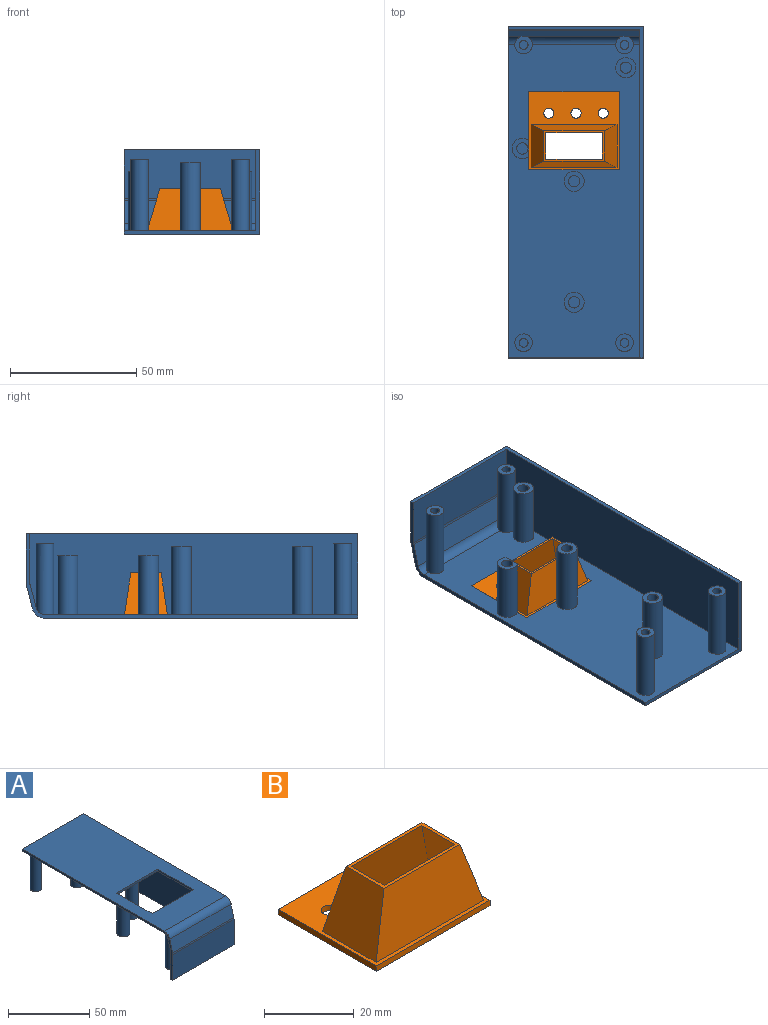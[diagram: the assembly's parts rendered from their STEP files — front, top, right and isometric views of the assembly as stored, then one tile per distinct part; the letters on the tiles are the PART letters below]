
ASSEMBLY  parts=2 mates=1
PART A: 51 faces, bbox 53.5x131.5x33.5 mm
  f0: plane 124.13x52mm, normal (0,0,-1), area 5027mm2, adj f3,f9,f13,f14,f16,f18,f20,f30
  f1: plane 124.13x53.5mm, normal (0,0,1), area 5525mm2, adj f3,f4,f8,f38,f39,f40,f41,f50
  f2: plane 131.5x53.5mm, normal (0,0,-1), area 275.2mm2, adj f3,f7,f8,f12,f13,f50
  f3: plane 53.5x33.5mm, normal (0,1,0), area 128.3mm2, adj f0,f1,f2,f8,f13,f50
  f4: cylinder r=5mm len=53.5mm, axis (-1,0,0), area 352.3mm2, adj f1,f5,f8,f50
  f5: plane 53.5x9.14mm, normal (0,-0.97,0.25), area 505mm2, adj f4,f6,f8,f50
  f6: cylinder r=5mm len=53.5mm, axis (-1,0,0), area 67.9mm2, adj f5,f7,f8,f50
  f7: plane 53.5x19.36mm, normal (0,-1,0), area 1035.9mm2, adj f2,f6,f8,f50
  f8: plane 131.5x33.5mm, normal (1,0,0), area 4378.7mm2, adj f1,f2,f3,f4,f5,f6,f7
  f9: cylinder r=3.5mm len=52mm, axis (-1,0,0), area 195.3mm2, adj f0,f10,f13,f18,f20,f50
  f10: plane 52x9.14mm, normal (0,0.97,-0.25), area 490.9mm2, adj f9,f11,f13,f50
  f11: cylinder r=3.5mm len=52mm, axis (-1,0,0), area 46.2mm2, adj f10,f12,f13,f50
  f12: plane 52x19.36mm, normal (0,1,0), area 1006.8mm2, adj f2,f11,f13,f50
  f13: plane 130x32mm, normal (-1,0,0), area 4139.3mm2, adj f0,f2,f3,f9,f10,f11,f12
  f14: cylinder r=3.5mm len=28.2mm, axis (0,0,1), area 620.2mm2, adj f0,f15
  f15: plane 7x7mm, normal (0,0,-1), area 28.9mm2, adj f14,f28
  f16: cylinder r=3.5mm len=28.2mm, axis (0,0,1), area 620.2mm2, adj f0,f17
  f17: plane 7x7mm, normal (0,0,-1), area 28.9mm2, adj f16,f26
  f18: cylinder r=3.5mm len=28.2mm, axis (0,0,1), area 608.4mm2, adj f0,f9,f19
  f19: plane 7x7mm, normal (0,0,-1), area 28.9mm2, adj f18,f24
  f20: cylinder r=3.5mm len=28.2mm, axis (0,0,1), area 608.4mm2, adj f0,f9,f21
  f21: plane 7x7mm, normal (0,0,-1), area 28.9mm2, adj f20,f22
  f22: cylinder r=1.75mm len=10mm, axis (0,0,-1), area 110mm2, adj f21,f23
  f23: plane 3.5x3.5mm, normal (0,0,-1), area 9.6mm2, adj f22
  f24: cylinder r=1.75mm len=10mm, axis (0,0,-1), area 110mm2, adj f19,f25
  f25: plane 3.5x3.5mm, normal (0,0,-1), area 9.6mm2, adj f24
  f26: cylinder r=1.75mm len=10mm, axis (0,0,-1), area 110mm2, adj f17,f27
  f27: plane 3.5x3.5mm, normal (0,0,-1), area 9.6mm2, adj f26
  f28: cylinder r=1.75mm len=10mm, axis (0,0,-1), area 110mm2, adj f15,f29
  f29: plane 3.5x3.5mm, normal (0,0,-1), area 9.6mm2, adj f28
  f30: cylinder r=4mm len=27mm, axis (0,0,1), area 678.6mm2, adj f0,f31
  f31: plane 8x8mm, normal (0,0,-1), area 34.4mm2, adj f30,f36
  f32: cylinder r=4mm len=27mm, axis (0,0,1), area 678.6mm2, adj f0,f33
  f33: plane 8x8mm, normal (0,0,-1), area 34.4mm2, adj f32,f34
  f34: cylinder r=2.25mm len=10mm, axis (0,0,-1), area 141.4mm2, adj f33,f35
  f35: plane 4.5x4.5mm, normal (0,0,-1), area 15.9mm2, adj f34
  f36: cylinder r=2.25mm len=10mm, axis (0,0,-1), area 141.4mm2, adj f31,f37
  f37: plane 4.5x4.5mm, normal (0,0,-1), area 15.9mm2, adj f36
  f38: plane 36x1.5mm, normal (0,1,0), area 54mm2, adj f0,f1,f39,f41
  f39: plane 31x1.5mm, normal (-1,0,0), area 46.5mm2, adj f0,f1,f38,f40
  f40: plane 36x1.5mm, normal (0,-1,0), area 54mm2, adj f0,f1,f39,f41
  f41: plane 31x24.9mm, normal (1,0,0), area 192.6mm2, adj f0,f1,f38,f40,f42,f43
  f42: cylinder r=4mm len=23.4mm, axis (0,0,1), area 420.4mm2, adj f0,f41,f43
  f43: plane 8x6.5mm, normal (0,0,-1), area 27.8mm2, adj f41,f42,f48
  f44: cylinder r=4mm len=23.4mm, axis (0,0,1), area 588.1mm2, adj f0,f45
  f45: plane 8x8mm, normal (0,0,-1), area 34.4mm2, adj f44,f46
  f46: cylinder r=2.25mm len=5mm, axis (0,0,-1), area 70.7mm2, adj f45,f47
  f47: plane 4.5x4.5mm, normal (0,0,-1), area 15.9mm2, adj f46
  f48: cylinder r=2.25mm len=5mm, axis (0,0,-1), area 70.7mm2, adj f43,f49
  f49: plane 4.5x4.5mm, normal (0,0,-1), area 15.9mm2, adj f48
  f50: plane 131.5x33.5mm, normal (-1,0,0), area 239.4mm2, adj f0,f1,f2,f3,f4,f5,f6,f7
PART B: 66 faces, bbox 36x31x18 mm
  f0: plane 36x31mm, normal (0,0,-1), area 561.9mm2, adj f1,f2,f3,f4,f5,f6,f7,f18
  f1: plane 36x1.5mm, normal (0,-1,0), area 54mm2, adj f0,f2,f7,f8
  f2: plane 31x1.5mm, normal (1,0,0), area 46.5mm2, adj f0,f1,f3,f8
  f3: plane 36x1.5mm, normal (0,1,0), area 54mm2, adj f0,f2,f7,f8
  f4: cylinder r=2mm len=4mm, axis (0,0,-1), area 18.8mm2, adj f0,f8
  f5: cylinder r=2mm len=4mm, axis (0,0,-1), area 18.8mm2, adj f0,f8
  f6: cylinder r=2mm len=4mm, axis (0,0,-1), area 18.8mm2, adj f0,f8
  f7: plane 31x1.5mm, normal (-1,0,0), area 46.5mm2, adj f0,f1,f3,f8
  f8: plane 36x31mm, normal (0,0,1), area 500.3mm2, adj f1,f2,f3,f4,f5,f6,f7,f10
  f9: plane 24x12mm, normal (0,0,1), area 56.2mm2, adj f10,f11,f12,f13,f14,f15,f16,f17
  f10: plane 17x16.5mm, normal (0.96,0,0.29), area 250mm2, adj f8,f9,f11,f13
  f11: plane 34x16.5mm, normal (0,0.99,0.15), area 484mm2, adj f8,f9,f10,f12
  f12: plane 17x16.5mm, normal (-0.96,0,0.29), area 250mm2, adj f8,f9,f11,f13
  f13: plane 34x16.5mm, normal (0,-0.99,0.15), area 484mm2, adj f8,f9,f10,f12
  f14: plane 17.2x15.59mm, normal (-0.96,0,-0.29), area 233.4mm2, adj f9,f15,f17,f18
  f15: plane 32.75x17.2mm, normal (0,-0.99,-0.15), area 479.1mm2, adj f9,f14,f16,f19
  f16: plane 17.2x15.59mm, normal (0.96,0,-0.29), area 233.4mm2, adj f9,f15,f17,f20
  f17: plane 32.75x17.2mm, normal (0,0.99,-0.15), area 479.1mm2, adj f9,f14,f16,f21
  f18: plane 15.59x0.8mm, normal (-1,0,0), area 12.5mm2, adj f0,f14,f19,f21
  f19: plane 32.75x0.8mm, normal (0,-1,0), area 26.2mm2, adj f0,f15,f18,f20
  f20: plane 15.59x0.8mm, normal (1,0,0), area 12.5mm2, adj f0,f16,f19,f21
  f21: plane 32.75x0.8mm, normal (0,1,0), area 26.2mm2, adj f0,f17,f18,f20
  f22: plane 1.26x0.5mm, normal (0,1,0), area 0.6mm2, adj f0,f23,f33,f34
  f23: plane 1.31x0.5mm, normal (-1,0,0), area 0.7mm2, adj f0,f22,f24,f34
  f24: plane 0.5x0.43mm, normal (0,1,0), area 0.2mm2, adj f0,f23,f25,f34
  f25: plane 1.31x0.5mm, normal (1,0,0), area 0.7mm2, adj f0,f24,f26,f34
  f26: plane 1.25x0.5mm, normal (0,1,0), area 0.6mm2, adj f0,f25,f27,f34
  f27: plane 0.5x0.42mm, normal (1,0,0), area 0.2mm2, adj f0,f26,f28,f34
  f28: plane 1.25x0.5mm, normal (0,-1,0), area 0.6mm2, adj f0,f27,f29,f34
  f29: plane 1.3x0.5mm, normal (1,0,0), area 0.7mm2, adj f0,f28,f30,f34
  f30: plane 0.5x0.43mm, normal (0,-1,0), area 0.2mm2, adj f0,f29,f31,f34
  f31: plane 1.3x0.5mm, normal (-1,0,0), area 0.7mm2, adj f0,f30,f32,f34
  f32: plane 1.26x0.5mm, normal (0,-1,0), area 0.6mm2, adj f0,f31,f33,f34
  f33: plane 0.5x0.42mm, normal (-1,0,0), area 0.2mm2, adj f0,f22,f32,f34
  f34: plane 3.03x2.93mm, normal (0,0,-1), area 2.3mm2, adj f22,f23,f24,f25,f26,f27,f28,f29
  f35: plane 0.62x0.5mm, normal (1,0,0), area 0.3mm2, adj f0,f36,f38,f39
  f36: plane 2x0.5mm, normal (0,-1,0), area 1mm2, adj f0,f35,f37,f39
  f37: plane 0.62x0.5mm, normal (-1,0,0), area 0.3mm2, adj f0,f36,f38,f39
  f38: plane 2x0.5mm, normal (0,1,0), area 1mm2, adj f0,f35,f37,f39
  f39: plane 2x0.62mm, normal (0,0,-1), area 1.2mm2, adj f35,f36,f37,f38
  f40: extruded ~0.61x0.5mm, area 0.4mm2, adj f0,f41,f64,f65
  f41: extruded ~0.5x0.5mm, area 0.3mm2, adj f0,f40,f42,f65
  f42: extruded ~0.64x0.5mm, area 0.4mm2, adj f0,f41,f43,f65
  f43: extruded ~0.5x0.41mm, area 0.2mm2, adj f0,f42,f44,f65
  f44: extruded ~0.5x0.19mm, area 0.1mm2, adj f0,f43,f45,f65
  f45: extruded ~0.5x0.25mm, area 0.1mm2, adj f0,f44,f46,f65
  f46: extruded ~0.5x0.33mm, area 0.2mm2, adj f0,f45,f47,f65
  f47: extruded ~0.5x0.43mm, area 0.2mm2, adj f0,f46,f48,f65
  f48: extruded ~0.72x0.5mm, area 0.4mm2, adj f0,f47,f49,f65
  f49: plane 0.5x0.3mm, normal (-0.94,-0.34,0), area 0.2mm2, adj f0,f48,f50,f65
  f50: extruded ~0.82x0.5mm, area 0.4mm2, adj f0,f49,f51,f65
  f51: extruded ~0.68x0.5mm, area 0.4mm2, adj f0,f50,f52,f65
  f52: extruded ~0.55x0.5mm, area 0.3mm2, adj f0,f51,f53,f65
  f53: extruded ~0.53x0.5mm, area 0.3mm2, adj f0,f52,f54,f65
  f54: extruded ~0.59x0.5mm, area 0.3mm2, adj f0,f53,f55,f65
  f55: extruded ~0.5x0.44mm, area 0.2mm2, adj f0,f54,f56,f65
  f56: extruded ~0.5x0.21mm, area 0.1mm2, adj f0,f55,f57,f65
  f57: extruded ~0.5x0.25mm, area 0.1mm2, adj f0,f56,f58,f65
  f58: extruded ~0.5x0.37mm, area 0.2mm2, adj f0,f57,f59,f65
  f59: extruded ~0.52x0.5mm, area 0.3mm2, adj f0,f58,f60,f65
  f60: extruded ~0.5x0.43mm, area 0.2mm2, adj f0,f59,f61,f65
  f61: extruded ~0.5x0.4mm, area 0.2mm2, adj f0,f60,f62,f65
  f62: plane 0.5x0.33mm, normal (1,0,0), area 0.2mm2, adj f0,f61,f63,f65
  f63: extruded ~0.81x0.5mm, area 0.4mm2, adj f0,f62,f64,f65
  f64: extruded ~0.77x0.5mm, area 0.4mm2, adj f0,f40,f63,f65
  f65: plane 3.06x1.87mm, normal (0,0,-1), area 2mm2, adj f40,f41,f42,f43,f44,f45,f46,f47
PLACE A rot(axis=(1,0,0),180deg) t=(-124.65,42.55,66.94)mm
PLACE B t=(10.22,-46.87,33.44)mm
MATE fastened A.f39 <-> B.f2  axis (-1,0,0) through (-79.15,16.55,34.94)mm
